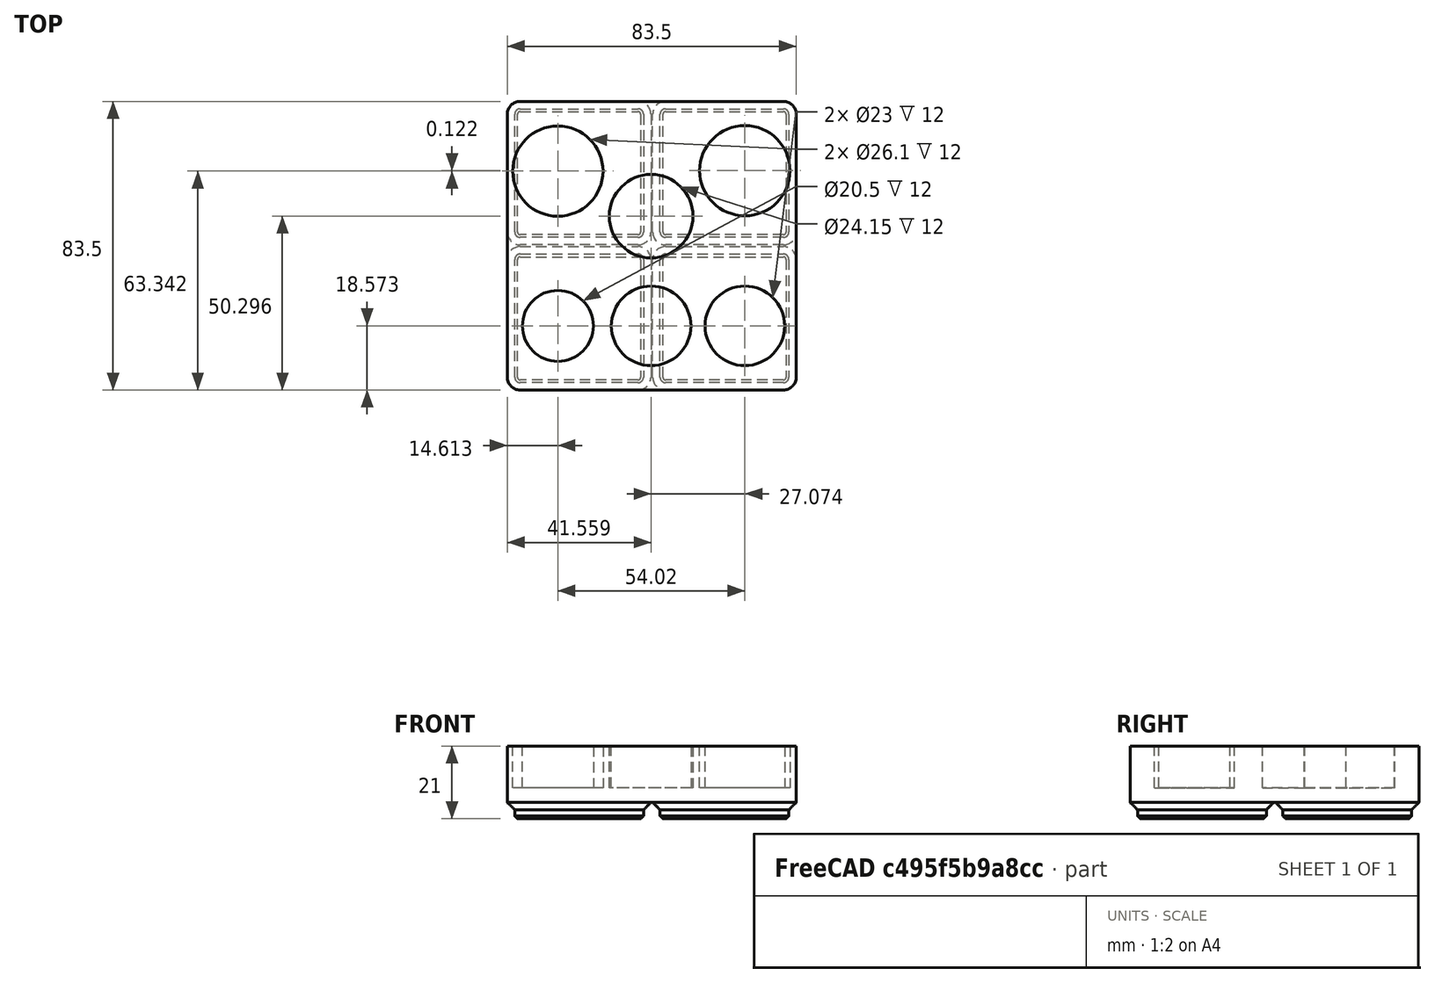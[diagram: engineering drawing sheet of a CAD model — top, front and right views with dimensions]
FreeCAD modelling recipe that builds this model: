
FCSTD DOCUMENT  (FreeCAD 0.21R33771 (Git))
Label: Sockets_Extras_I_gridfinity
License: All rights reserved
LicenseURL: http://en.wikipedia.org/wiki/All_rights_reserved
objects: PartDesign::FeaturePython×1, PartDesign::Plane×1, Sketcher::SketchObject×1, PartDesign::Pocket×1, PartDesign::Body×1
note: 6 computed .brp shape members not serialized (recipe doc carries the construction recipe); baked Part::Feature solids carry a one-line shape summary decoded from their .brp

FEATURE [PartDesign::FeaturePython] BinBlank  # WARN: FeaturePython — macro-defined, semantics opaque (R4)
  BaseProfileBottomChamfer = 0.8
  BaseProfileHeight = 4.75
  BaseProfileTopChamfer = 2.15
  BaseProfileVerticalSection = 1.8
  BinBottomRadius = 0.8
  BinOuterRadius = 3.75
  BinUnit = 41.5
  BinVerticalRadius = 1.6
  CustomHeight = 42
  GridSize = 42
  HeightUnitValue = 7
  HeightUnits = 3
  MagnetHoleDepth = 2.4
  MagnetHoleDiameter = 6.5
  MagnetHoleDistanceFromEdge = 8
  MagnetHoles = false
  NonStandardHeight = false
  ScrewHoleDepth = 6
  ScrewHoleDiameter = 3
  ScrewHoles = false
  SequentialBridgingLayerHeight = 0.2
  StackingLip = false
  StackingLipBottomChamfer = 0.7
  StackingLipTopChamfer = 1.5
  StackingLipTopLedge = 0.4
  StackingLipVerticalSection = 1.8
  Tolerance = 0.25
  TotalHeight = 21
  WallThickness = 1
  version = 0.5.0
  xGridUnits = 2
  xTotalWidth = 83.5
  yGridUnits = 2
  yTotalWidth = 83.5
FEATURE [PartDesign::Plane] DatumPlane
  Length = 105.3
  MapMode = 5
  ResizeMode = 0
  Support = -> [BinBlank]
  Width = 105.3
FEATURE [Sketcher::SketchObject] Sketch
  FullyConstrained = false
  MapMode = 5
  Support = -> [BinBlank]
  sketch-geometry (6):
    g0: Circle CenterX=-6.13673 CenterY=-2.17666 CenterZ=0 NormalX=0 NormalY=0 NormalZ=1 AngleXU=0 Radius=10.25
    g1: Circle CenterX=20.8086 CenterY=-2.17666 CenterZ=0 NormalX=0 NormalY=0 NormalZ=1 AngleXU=0 Radius=11.5
    g2: Circle CenterX=47.883 CenterY=-2.17666 CenterZ=0 NormalX=0 NormalY=0 NormalZ=1 AngleXU=0 Radius=11.5
    g3: Circle CenterX=20.8086 CenterY=29.5459 CenterZ=0 NormalX=0 NormalY=0 NormalZ=1 AngleXU=0 Radius=12.075
    g4: Circle CenterX=-6.13673 CenterY=42.5918 CenterZ=0 NormalX=0 NormalY=0 NormalZ=1 AngleXU=0 Radius=13.05
    g5: Circle CenterX=47.883 CenterY=42.7137 CenterZ=0 NormalX=0 NormalY=0 NormalZ=1 AngleXU=0 Radius=13.05
  constraints (6):
    c: Diameter(g2) = 23
    c: Diameter(g1) = 23
    c: Diameter(g0) = 20.5
    c: Diameter(g5) = 26.1
    c: Diameter(g3) = 24.15
    c: Diameter(g4) = 26.1
FEATURE [PartDesign::Pocket] Pocket
  BaseFeature = -> BinBlank
  Direction = (0,0,-1)
  Length = 12
  Length2 = 5
  Profile = -> Sketch
  ReferenceAxis = -> Sketch [N_Axis]
  Type = 0
FEATURE [PartDesign::Body] Body
  Group = -> [BinBlank,DatumPlane,Sketch,Pocket]
  Origin = -> Origin
  Tip = -> Pocket
